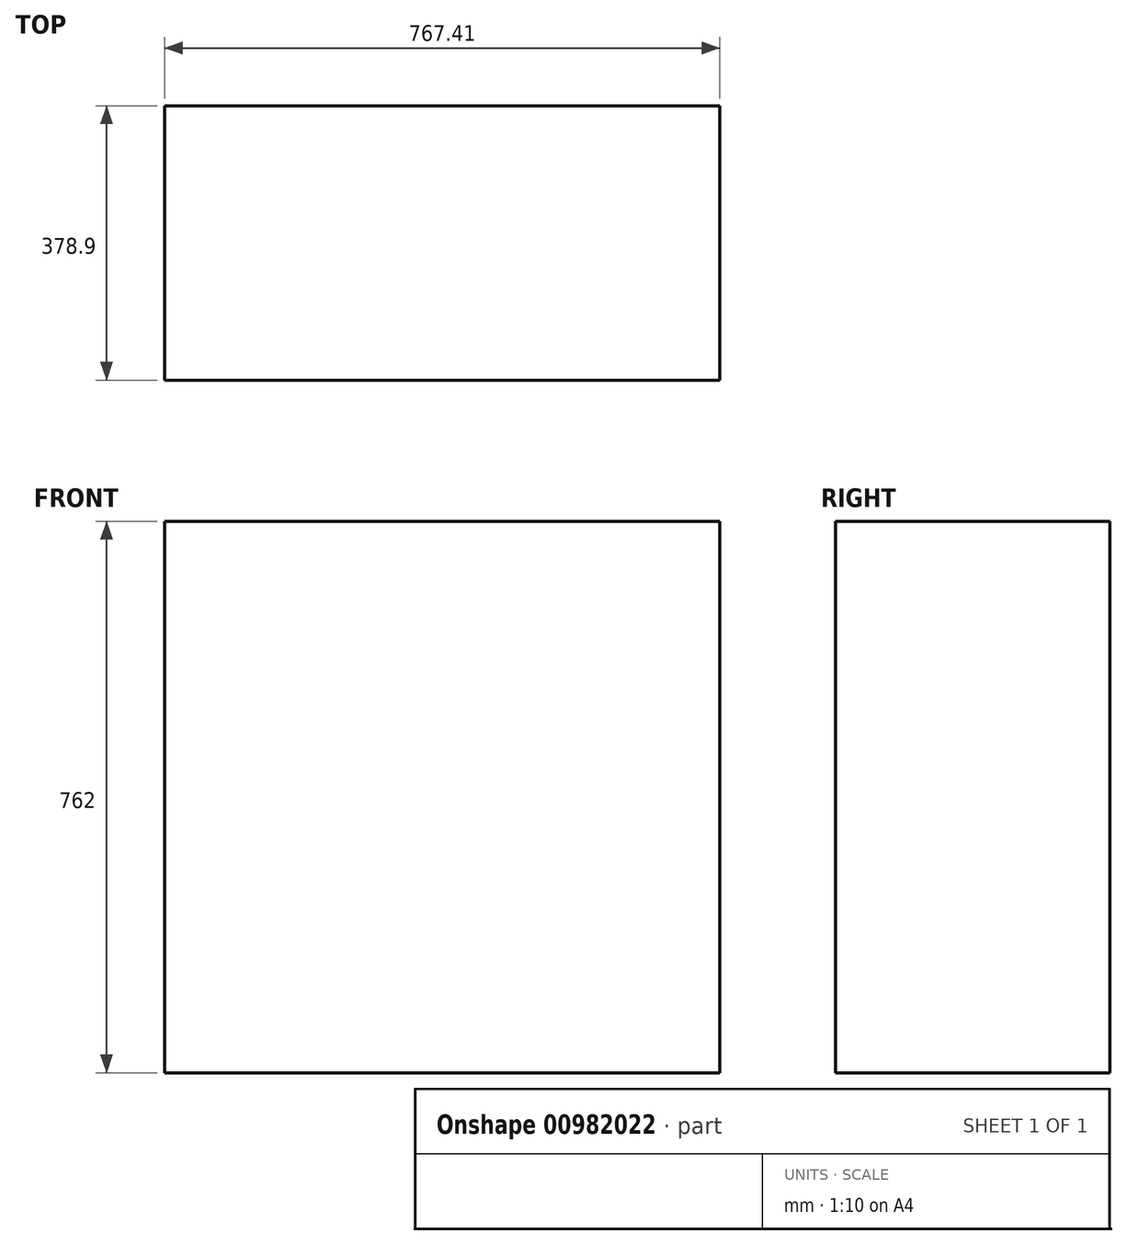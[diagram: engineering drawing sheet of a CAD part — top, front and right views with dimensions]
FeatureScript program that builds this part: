
annotation { "Feature Type Name" : "Feature", "Feature Type Description" : "" }
export const myFeature = defineFeature(function(context is Context, id is Id, definition is map)
    precondition{}
    {
        {
            var Q0;
            Q0=qCreatedBy(makeId("Top.planeOp"),FACE);
            var sketch = newSketch(context, id + "F0", { "sketchPlane" : qUnion([Q0])});
            skLineSegment(sketch, "E0.bottom", {"start": v(-788.25, 46.93) * mm, "end": v(-20.84, 46.93) * mm});
            skLineSegment(sketch, "E0.top", {"start": v(-788.25, -331.97) * mm, "end": v(-20.84, -331.97) * mm});
            skLineSegment(sketch, "E0.left", {"start": v(-788.25, 46.93) * mm, "end": v(-788.25, -331.97) * mm});
            skLineSegment(sketch, "E0.right", {"start": v(-20.84, 46.93) * mm, "end": v(-20.84, -331.97) * mm});
            skSolve(sketch);
        }
        {
            var Q0;
            Q0 = qSketchRegion(id + "F0", true);
            extrude(context, id + "F1", {"entities" : qUnion([Q0]), "depth" : 762 * mm, "offsetDistance" : 25.4 * mm});
        }
    });
